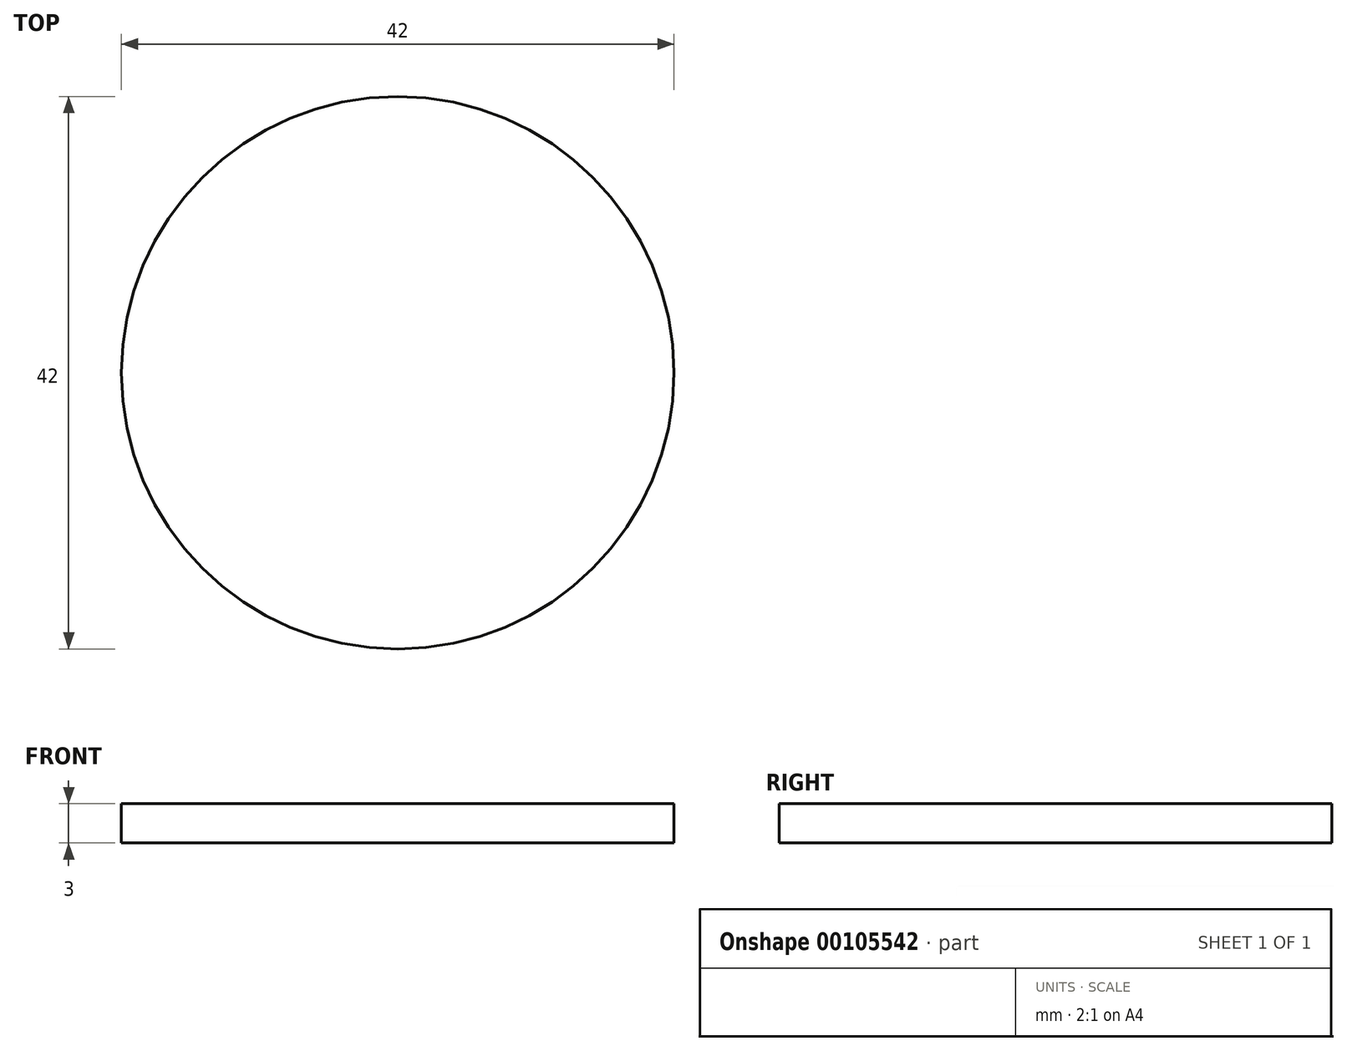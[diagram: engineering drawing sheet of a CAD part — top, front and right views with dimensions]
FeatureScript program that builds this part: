
annotation { "Feature Type Name" : "Feature", "Feature Type Description" : "" }
export const myFeature = defineFeature(function(context is Context, id is Id, definition is map)
    precondition{}
    {
        {
            var Q0;
            Q0=qCreatedBy(makeId("Top.planeOp"),FACE);
            var sketch = newSketch(context, id + "F0", { "sketchPlane" : qUnion([Q0])});
            skCircle(sketch, "E0", {"center": v(0, 0) * mm, "radius": 21 * mm});
            skSolve(sketch);
        }
        {
            var Q0;
            Q0 = qSketchRegion(id + "F0", true);
            extrude(context, id + "F1", {"entities" : qUnion([Q0]), "depth" : 3 * mm});
        }
    });
